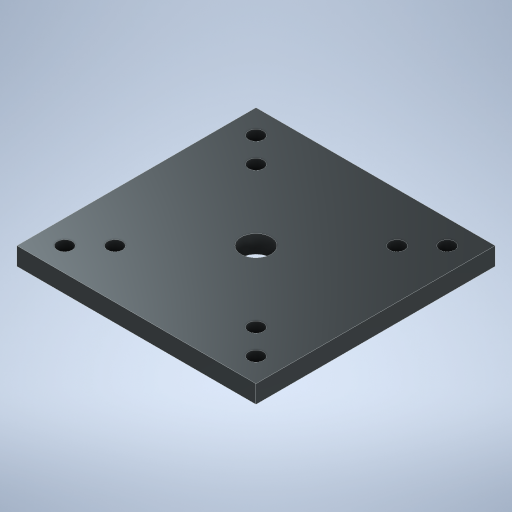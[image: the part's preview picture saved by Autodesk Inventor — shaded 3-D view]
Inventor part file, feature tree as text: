
AUTODESK INVENTOR PART (.ipt)
format: ipt  version: 2023 (Build 270158000, 158)  size: 269,312 bytes
history: native  units: mm
features: sketch x4, hole x3, other x1, extrude x1
ambient origin geometry x8: Origin, YZ Plane, XZ Plane, XY Plane, X Axis, Y Axis, Z Axis, Center Point
bodies: Body1 (feature_tree)
feature tree (9):
  other  "Sólido1"
  extrude  "Extrusão1"  Depth=80.0mm
  hole  "Furo1"  [1 undecoded]
  hole  "Furo2"  [1 undecoded]
  hole  "Furo3"  [1 undecoded]
  sketch  "Esboço1"  dims[d0=80.0mm d1=80.0mm]
  sketch  "Esboço2"  dims[d2=6.0mm d3=0.0mm d4=47.2mm]
  sketch  "Esboço3"  dims[d5=47.2mm d6=47.2mm]
  sketch  "Esboço4"  dims[d7=47.2mm d8=0.0mm d9=0.0mm d10=80.0mm d11=16.4mm d12=16.4mm d13=5.0mm d14=6.0mm d15=4.0mm d16=2.0mm d17=90.0deg d18=0.5mm d19=20.594885mm d20=8.0mm d21=8.0mm d22=8.0mm d23=8.0mm d24=8.0mm d25=8.0mm d26=8.0mm d27=8.0mm d28=5.0mm d29=6.0mm d30=4.0mm d31=2.0mm d32=90.0deg d33=8.0mm d34=20.594885mm d35=80.0mm d36=40.0mm d37=40.0mm d38=10.0mm d39=6.0mm d40=4.0mm d41=2.0mm d42=90.0deg d43=8.0mm d44=20.594885mm]
note: 3 required parameter values undecoded (feature->parameter linkage not recoverable at this tier; creation-order binding heuristic only, values carry confidence <= 0.55)
